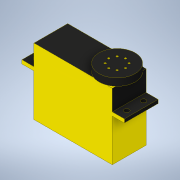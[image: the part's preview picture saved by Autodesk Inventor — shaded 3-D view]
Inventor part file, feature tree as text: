
AUTODESK INVENTOR PART (.ipt)
format: ipt  version: 2020 (Build 240168000, 168)  size: 198,144 bytes
history: native  units: mm
features: extrude x5, sketch x4
ambient origin geometry x8: Origin, YZ Plane, XZ Plane, XY Plane, X Axis, Y Axis, Z Axis, Center Point
bodies: Solid1 (feature_tree)
feature tree (9):
  extrude  "Extrusion1"  Depth=28.0mm
  extrude  "Extrusion2"  Depth=10.0mm
  extrude  "Extrusion3"  Depth=6.0mm TaperAngle=0.0deg
  extrude  "Extrusion4"  Depth=17.0mm
  extrude  "Extrusion5"  Depth=17.0mm TaperAngle=360.0deg
  sketch  "Sketch2"  dims[d0=65.0mm d1=28.0mm]
  sketch  "Sketch3"  dims[d2=55.0mm d3=0.0mm d4=10.0mm]
  sketch  "Sketch4"  dims[d5=30.0mm d6=6.0mm d7=0.0mm]
  sketch  "Sketch5"  dims[d12=1.6mm d14=7.0mm d15=80.0mm d17=360.0deg d19=3.5mm d20=0.0mm d21=4.0mm d22=14.0mm d23=7.0mm d26=20.0mm d27=0.0mm d28=14.0mm d29=5.0mm d30=5.0mm d31=5.0mm d32=5.0mm d33=17.0mm d34=0.0mm]
